# Revit family: 143_HL310NPr-3000
name_source: partatom
category: Instalační zařizovací předměty
revit_build: Autodesk Revit 2016 (Build: 20150714_1515(x64)
units: mm (PartAtom-declared; Revit-internal decimal feet)

## family parameters
Bod výpočtu místnosti = Ano
Kóta kulaté spojky = Použít průměr
Nadpis OmniClass = Deck Waste Water Drains
Ořezat dutým tvarem při načtení = Ne
Sdílené = Ano
Typ součásti = Normální
Vždy vertikální = Ano
Založené na pracovní rovině = Ne
Číslo OmniClass = 23.70.50.21.24.14

## types (1)
- HL310NPr-3000
    EAN = 9003076016440
    Klíčová poznámka = HL310NPr-3000
    Komentáře k typům = HL310NPr-3000 Трап для внутренних помещений DN50/75/110 вертикальный с запахозапирающим устройством Primus, 121х121мм KLICK-KLACK/115х115мм.
    Model = HL310NPr-3000
    Popis = Трапы для внутренних помещений
    Připojení CW = Ne
    Připojení HW = Ne
    Připojení odpadu = Ano
    Připojení ventilace = Ne
    URL = http://www.hutterer-lechner.com
    Výrobce = HL Hutterer & Lechner GmbH
    ВЕС = 0,74 [kg]
    ВЫСОТА МОНТАЖА = 154 mm
    МАКСИМАЛЬНАЯ НАГРУЗКА КЛАССА = K3 - 300 kg
    МАТЕРИАЛ = PE
    НАСАДКА = 10-80 mm / 121 x 121 mm / PP-V2A
    ПРОИЗВОДИТЕЛЬНОСТЬ = 0,5 l/s
    ПРОПУСКНАЯ СПОСОБНОСТЬ = 0.5 L/s
    РАЗМЕР = DN50/75/110
    РЕШЁТКА = 115 x 115 mm / V2A

## geometry (parser evidence)
native form markers: Sweep x34
no freeform markers — native parametric forms only
